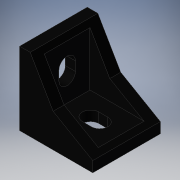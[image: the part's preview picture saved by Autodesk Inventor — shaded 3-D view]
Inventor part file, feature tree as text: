
AUTODESK INVENTOR PART (.ipt)
format: ipt  version: 2019 (Build 230136000, 136)  size: 157,696 bytes
history: native  units: mm
features: other x35, extrude x6, sketch x6
ambient origin geometry x8: Origin, YZ Plane, XZ Plane, XY Plane, X Axis, Y Axis, Z Axis, Center Point
bodies: Solid1 (feature_tree)
feature tree (47):
  extrude  "Extrusion1"  Depth=25.0mm TaperAngle=0.0deg
  extrude  "Extrusion2"  Depth=7.5mm TaperAngle=0.0deg
  extrude  "Extrusion3"  Depth=2.0mm TaperAngle=0.0deg
  extrude  "Extrusion4"  [1 undecoded]
  extrude  "Extrusion5"  [1 undecoded]
  extrude  "Extrusion6"  [1 undecoded]
  other  "GUS_4500_1_XY"
  other  "GUS_4500_1_YZ"
  other  "GUS_4500_1_ZX"
  other  "GUS_4500_1_X"
  other  "GUS_4500_1_Y"
  other  "GUS_4500_1_Z"
  other  "GUS_4500_1_Center"
  other  "GUS_4500_12_XY"
  other  "GUS_4500_12_YZ"
  other  "GUS_4500_12_ZX"
  other  "GUS_4500_12_X"
  other  "GUS_4500_12_Y"
  other  "GUS_4500_12_Z"
  other  "GUS_4500_12_Center"
  other  "GUS_4500_2_XY"
  other  "GUS_4500_2_YZ"
  other  "GUS_4500_2_ZX"
  other  "GUS_4500_2_X"
  other  "GUS_4500_2_Y"
  other  "GUS_4500_2_Z"
  other  "GUS_4500_2_Center"
  other  "GUS_4500_23_XY"
  other  "GUS_4500_23_YZ"
  other  "GUS_4500_23_ZX"
  other  "GUS_4500_23_X"
  other  "GUS_4500_23_Y"
  other  "GUS_4500_23_Z"
  other  "GUS_4500_23_Center"
  other  "p1_XY"
  other  "p1_YZ"
  other  "p1_ZX"
  other  "p1_X"
  other  "p1_Y"
  other  "p1_Z"
  other  "p1_Center"
  sketch  "Skizze_1"  dims[d0=37.0mm d1=0.0mm d2=25.0mm d3=0.0mm]
  sketch  "Skizze_2"  dims[d4=7.5mm d5=0.0mm d6=7.5mm d7=0.0mm]
  sketch  "Skizze_3"  dims[d8=2.0mm d9=0.0mm d10=2.0mm d11=0.0mm]
  sketch  "Skizze_4"  dims[d12=0.0mm d13=0.0mm d14=0.0mm d15=0.0mm d16=0.0mm]
  sketch  "Skizze_5"
  sketch  "Skizze_6"
note: 3 required parameter values undecoded (feature->parameter linkage not recoverable at this tier; creation-order binding heuristic only, values carry confidence <= 0.55)
